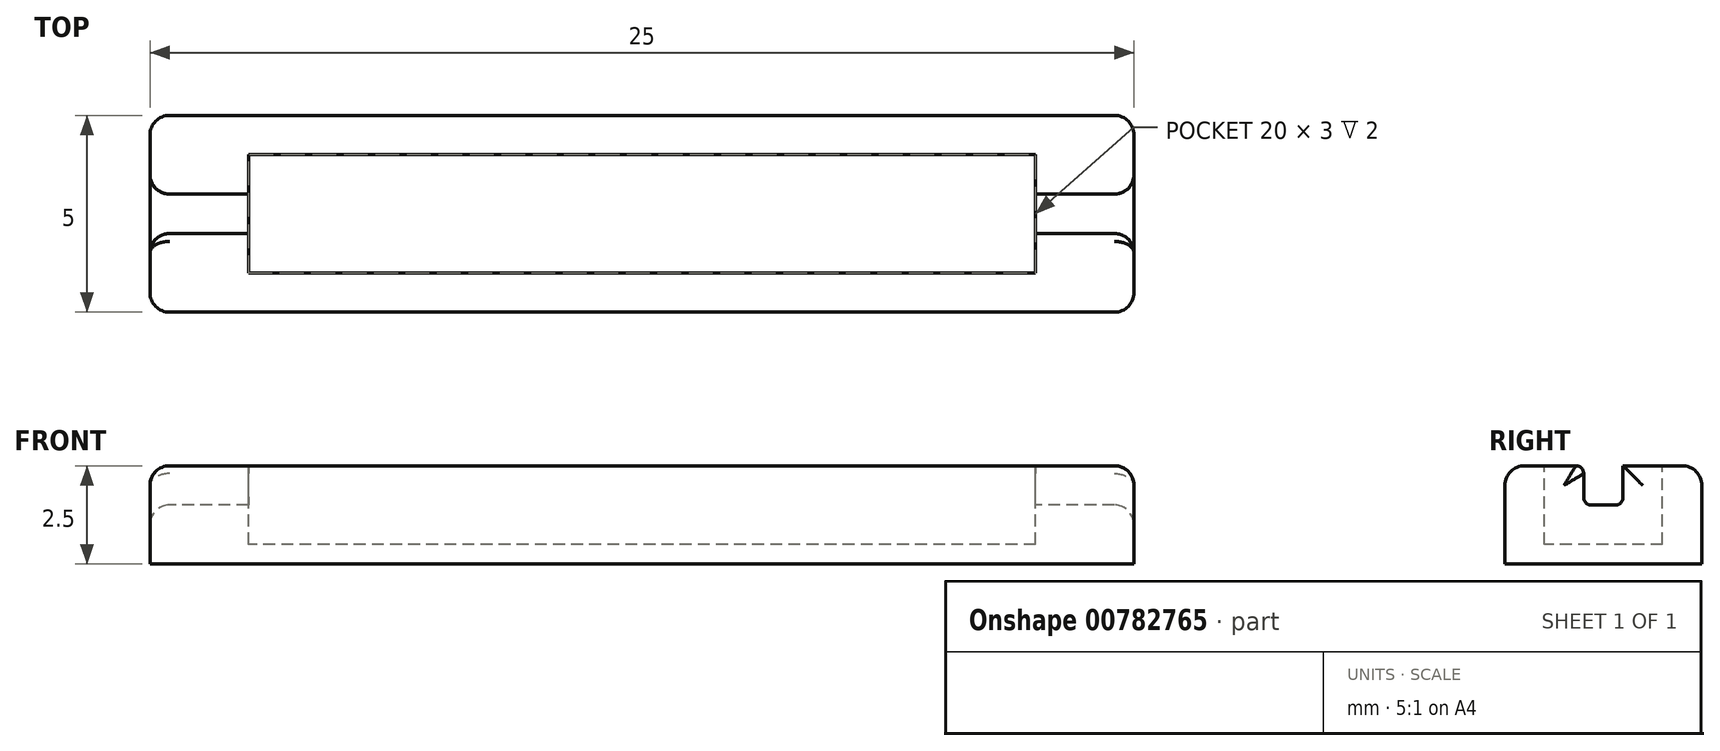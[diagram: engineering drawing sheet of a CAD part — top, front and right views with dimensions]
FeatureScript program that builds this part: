
annotation { "Feature Type Name" : "Feature", "Feature Type Description" : "" }
export const myFeature = defineFeature(function(context is Context, id is Id, definition is map)
    precondition{}
    {
        {
            var Q0;
            Q0=qCreatedBy(makeId("Top.planeOp"),FACE);
            var sketch = newSketch(context, id + "F0", { "sketchPlane" : qUnion([Q0])});
            skLineSegment(sketch, "E0.bottom", {"start": v(12.5, 2.5) * mm, "end": v(-12.5, 2.5) * mm});
            skLineSegment(sketch, "E0.top", {"start": v(12.5, -2.5) * mm, "end": v(-12.5, -2.5) * mm});
            skLineSegment(sketch, "E0.left", {"start": v(12.5, 2.5) * mm, "end": v(12.5, -2.5) * mm});
            skLineSegment(sketch, "E0.right", {"start": v(-12.5, 2.5) * mm, "end": v(-12.5, -2.5) * mm});
            skPoint(sketch, "E0.middle", {"position": v(0, 0) * mm});
            skSolve(sketch);
        }
        {
            var Q0;
            Q0=makeQuery(id+"F0.imprint","IMPRINT",FACE,{"disambiguationData":[TD([[makeQuery(id+"F0.imprint","IMPRINT",EDGE,{"derivedFrom":sQuery(id+"F0.wireOp",EDGE,"E0.bottom")}),1.0]])]});
            extrude(context, id + "F1", {"entities" : qUnion([Q0]), "depth" : 2.5 * mm, "offsetDistance" : 25.4 * mm});
        }
        {
            var Q0;
            Q0=makeQuery(id+"F1.opExtrude","CAP_FACE",FACE,{"disambiguationData":[OSD([sQuery(id+"F0.wireOp",EDGE,"E0.bottom"),sQuery(id+"F0.wireOp",EDGE,"E0.top"),sQuery(id+"F0.wireOp",EDGE,"E0.left"),sQuery(id+"F0.wireOp",EDGE,"E0.right")])],"isStart":false});
            var sketch = newSketch(context, id + "F2", { "sketchPlane" : qUnion([Q0])});
            skLineSegment(sketch, "E1.bottom", {"start": v(10, 1.5) * mm, "end": v(-10, 1.5) * mm});
            skLineSegment(sketch, "E1.top", {"start": v(10, -1.5) * mm, "end": v(-10, -1.5) * mm});
            skLineSegment(sketch, "E1.left", {"start": v(10, 1.5) * mm, "end": v(10, -1.5) * mm});
            skLineSegment(sketch, "E1.right", {"start": v(-10, 1.5) * mm, "end": v(-10, -1.5) * mm});
            skPoint(sketch, "E1.middle", {"position": v(0, 0) * mm});
            skSolve(sketch);
        }
        {
            var Q0;
            Q0=makeQuery(id+"F2.imprint","IMPRINT",FACE,{"disambiguationData":[TD([[makeQuery(id+"F2.imprint","IMPRINT",EDGE,{"derivedFrom":sQuery(id+"F2.wireOp",EDGE,"E1.bottom")}),1.0]])]});
            extrude(context, id + "F3", {"entities" : qUnion([Q0]), "operationType" : NewBodyOperationType.REMOVE, "oppositeDirection" : true, "depth" : 2 * mm, "offsetDistance" : 25.4 * mm});
        }
        {
            var Q0;
            Q0=makeQuery(id+"F1.opExtrude","CAP_FACE",FACE,{"disambiguationData":[OSD([sQuery(id+"F0.wireOp",EDGE,"E0.bottom"),sQuery(id+"F0.wireOp",EDGE,"E0.top"),sQuery(id+"F0.wireOp",EDGE,"E0.left"),sQuery(id+"F0.wireOp",EDGE,"E0.right")])],"isStart":false});
            var sketch = newSketch(context, id + "F4", { "sketchPlane" : qUnion([Q0])});
            skLineSegment(sketch, "E2.bottom", {"start": v(12.5, -0.5) * mm, "end": v(-12.5, -0.5) * mm});
            skLineSegment(sketch, "E2.top", {"start": v(12.5, 0.5) * mm, "end": v(-12.5, 0.5) * mm});
            skLineSegment(sketch, "E2.left", {"start": v(12.5, -0.5) * mm, "end": v(12.5, 0.5) * mm});
            skLineSegment(sketch, "E2.right", {"start": v(-12.5, -0.5) * mm, "end": v(-12.5, 0.5) * mm});
            skPoint(sketch, "E2.middle", {"position": v(0, 0) * mm});
            skSolve(sketch);
        }
        {
            var Q0;
            {var subQ0=sQuery(id+"F4.wireOp",EDGE,"E2.right");Q0=makeQuery(id+"F4.imprint","IMPRINT",FACE,{"disambiguationData":[TD([[makeQuery(id+"F4.imprint","IMPRINT",EDGE,{"derivedFrom":subQ0}),1.0]])]});}
            var Q1;
            {var subQ0=sQuery(id+"F4.wireOp",EDGE,"E2.left");Q1=makeQuery(id+"F4.imprint","IMPRINT",FACE,{"disambiguationData":[TD([[makeQuery(id+"F4.imprint","IMPRINT",EDGE,{"derivedFrom":subQ0}),-1.0]])]});}
            extrude(context, id + "F5", {"entities" : qUnion([Q0, Q1]), "operationType" : NewBodyOperationType.REMOVE, "oppositeDirection" : true, "depth" : 1 * mm, "offsetDistance" : 25.4 * mm});
        }
        {
            var Q0;
            {var subQ0=sQuery(id+"F4.wireOp",EDGE,"E2.bottom");Q0=makeQuery(id+"F5.boolean.opBoolean","COPY",EDGE,{"derivedFrom":makeQuery(id+"F5.opExtrude","CAP_EDGE",EDGE,{"disambiguationData":[OSD([subQ0]),TDD([makeQuery(id+"F4.imprint","IMPRINT",EDGE,{"disambiguationData":[TD([[makeQuery(id+"F4.imprint","INTERSECT",VERTEX,{"derivedFrom":[makeQuery(id+"F3.boolean.opBoolean","COPY",EDGE,{"derivedFrom":makeQuery(id+"F3.opExtrude","CAP_EDGE",EDGE,{"disambiguationData":[OSD([sQuery(id+"F2.wireOp",EDGE,"E1.right")])],"isStart":true})}),subQ0]}),-1.0]])],"derivedFrom":subQ0})])],"isStart":false})});}
            var Q1;
            {var subQ0=sQuery(id+"F4.wireOp",EDGE,"E2.top");Q1=makeQuery(id+"F5.boolean.opBoolean","COPY",EDGE,{"derivedFrom":makeQuery(id+"F5.opExtrude","CAP_EDGE",EDGE,{"disambiguationData":[OSD([subQ0]),TDD([makeQuery(id+"F4.imprint","IMPRINT",EDGE,{"disambiguationData":[TD([[makeQuery(id+"F4.imprint","INTERSECT",VERTEX,{"derivedFrom":[makeQuery(id+"F3.boolean.opBoolean","COPY",EDGE,{"derivedFrom":makeQuery(id+"F3.opExtrude","CAP_EDGE",EDGE,{"disambiguationData":[OSD([sQuery(id+"F2.wireOp",EDGE,"E1.right")])],"isStart":true})}),subQ0]}),-1.0]])],"derivedFrom":subQ0})])],"isStart":false})});}
            var Q2;
            Q2=makeQuery(id+"F5.boolean.opBoolean","COPY",EDGE,{"derivedFrom":makeQuery(id+"F5.opExtrude","SWEPT_EDGE",EDGE,{"disambiguationData":[OSD([sQuery(id+"F2.wireOp",EDGE,"E1.right"),sQuery(id+"F4.wireOp",EDGE,"E2.bottom")])]})});
            var Q3;
            {var subQ0=sQuery(id+"F4.wireOp",EDGE,"E2.bottom");Q3=makeQuery(id+"F5.boolean.opBoolean","COPY",EDGE,{"derivedFrom":makeQuery(id+"F5.opExtrude","CAP_EDGE",EDGE,{"disambiguationData":[OSD([subQ0]),TDD([makeQuery(id+"F4.imprint","IMPRINT",EDGE,{"disambiguationData":[TD([[makeQuery(id+"F4.imprint","INTERSECT",VERTEX,{"derivedFrom":[makeQuery(id+"F3.boolean.opBoolean","COPY",EDGE,{"derivedFrom":makeQuery(id+"F3.opExtrude","CAP_EDGE",EDGE,{"disambiguationData":[OSD([sQuery(id+"F2.wireOp",EDGE,"E1.left")])],"isStart":true})}),subQ0]}),1.0]])],"derivedFrom":subQ0})])],"isStart":false})});}
            var Q4;
            {var subQ0=sQuery(id+"F4.wireOp",EDGE,"E2.top");Q4=makeQuery(id+"F5.boolean.opBoolean","COPY",EDGE,{"derivedFrom":makeQuery(id+"F5.opExtrude","CAP_EDGE",EDGE,{"disambiguationData":[OSD([subQ0]),TDD([makeQuery(id+"F4.imprint","IMPRINT",EDGE,{"disambiguationData":[TD([[makeQuery(id+"F4.imprint","INTERSECT",VERTEX,{"derivedFrom":[makeQuery(id+"F3.boolean.opBoolean","COPY",EDGE,{"derivedFrom":makeQuery(id+"F3.opExtrude","CAP_EDGE",EDGE,{"disambiguationData":[OSD([sQuery(id+"F2.wireOp",EDGE,"E1.left")])],"isStart":true})}),subQ0]}),1.0]])],"derivedFrom":subQ0})])],"isStart":false})});}
            var Q5;
            Q5=makeQuery(id+"F5.boolean.opBoolean","COPY",EDGE,{"derivedFrom":makeQuery(id+"F5.opExtrude","CAP_EDGE",EDGE,{"disambiguationData":[OSD([sQuery(id+"F2.wireOp",EDGE,"E1.left")])],"isStart":false})});
            var Q6;
            Q6=makeQuery(id+"F5.boolean.opBoolean","COPY",EDGE,{"derivedFrom":makeQuery(id+"F5.opExtrude","SWEPT_EDGE",EDGE,{"disambiguationData":[OSD([sQuery(id+"F0.wireOp",EDGE,"E0.left"),sQuery(id+"F4.wireOp",EDGE,"E2.bottom"),sQuery(id+"F4.wireOp",EDGE,"E2.left")])]})});
            var Q7;
            Q7=makeQuery(id+"F5.boolean.opBoolean","COPY",EDGE,{"derivedFrom":makeQuery(id+"F5.opExtrude","SWEPT_EDGE",EDGE,{"disambiguationData":[OSD([sQuery(id+"F0.wireOp",EDGE,"E0.right"),sQuery(id+"F4.wireOp",EDGE,"E2.top"),sQuery(id+"F4.wireOp",EDGE,"E2.right")])]})});
            var Q8;
            {var subQ0=sQuery(id+"F4.wireOp",EDGE,"E2.top");Q8=makeQuery(id+"F5.boolean.opBoolean","COPY",EDGE,{"derivedFrom":makeQuery(id+"F5.opExtrude","CAP_EDGE",EDGE,{"disambiguationData":[OSD([subQ0]),TDD([makeQuery(id+"F4.imprint","IMPRINT",EDGE,{"disambiguationData":[TD([[makeQuery(id+"F4.imprint","INTERSECT",VERTEX,{"derivedFrom":[makeQuery(id+"F3.boolean.opBoolean","COPY",EDGE,{"derivedFrom":makeQuery(id+"F3.opExtrude","CAP_EDGE",EDGE,{"disambiguationData":[OSD([sQuery(id+"F2.wireOp",EDGE,"E1.right")])],"isStart":true})}),subQ0]}),-1.0]])],"derivedFrom":subQ0})])],"isStart":true})});}
            var Q9;
            {var subQ0=sQuery(id+"F4.wireOp",EDGE,"E2.bottom");Q9=makeQuery(id+"F5.boolean.opBoolean","COPY",EDGE,{"derivedFrom":makeQuery(id+"F5.opExtrude","CAP_EDGE",EDGE,{"disambiguationData":[OSD([subQ0]),TDD([makeQuery(id+"F4.imprint","IMPRINT",EDGE,{"disambiguationData":[TD([[makeQuery(id+"F4.imprint","INTERSECT",VERTEX,{"derivedFrom":[makeQuery(id+"F3.boolean.opBoolean","COPY",EDGE,{"derivedFrom":makeQuery(id+"F3.opExtrude","CAP_EDGE",EDGE,{"disambiguationData":[OSD([sQuery(id+"F2.wireOp",EDGE,"E1.right")])],"isStart":true})}),subQ0]}),-1.0]])],"derivedFrom":subQ0})])],"isStart":true})});}
            var Q10;
            {var subQ0=sQuery(id+"F4.wireOp",EDGE,"E2.top");Q10=makeQuery(id+"F5.boolean.opBoolean","COPY",EDGE,{"derivedFrom":makeQuery(id+"F5.opExtrude","CAP_EDGE",EDGE,{"disambiguationData":[OSD([subQ0]),TDD([makeQuery(id+"F4.imprint","IMPRINT",EDGE,{"disambiguationData":[TD([[makeQuery(id+"F4.imprint","INTERSECT",VERTEX,{"derivedFrom":[makeQuery(id+"F3.boolean.opBoolean","COPY",EDGE,{"derivedFrom":makeQuery(id+"F3.opExtrude","CAP_EDGE",EDGE,{"disambiguationData":[OSD([sQuery(id+"F2.wireOp",EDGE,"E1.left")])],"isStart":true})}),subQ0]}),1.0]])],"derivedFrom":subQ0})])],"isStart":true})});}
            var Q11;
            {var subQ0=sQuery(id+"F4.wireOp",EDGE,"E2.bottom");Q11=makeQuery(id+"F5.boolean.opBoolean","COPY",EDGE,{"derivedFrom":makeQuery(id+"F5.opExtrude","CAP_EDGE",EDGE,{"disambiguationData":[OSD([subQ0]),TDD([makeQuery(id+"F4.imprint","IMPRINT",EDGE,{"disambiguationData":[TD([[makeQuery(id+"F4.imprint","INTERSECT",VERTEX,{"derivedFrom":[makeQuery(id+"F3.boolean.opBoolean","COPY",EDGE,{"derivedFrom":makeQuery(id+"F3.opExtrude","CAP_EDGE",EDGE,{"disambiguationData":[OSD([sQuery(id+"F2.wireOp",EDGE,"E1.left")])],"isStart":true})}),subQ0]}),1.0]])],"derivedFrom":subQ0})])],"isStart":true})});}
            var Q12;
            {var subQ2=sQuery(id+"F2.wireOp",EDGE,"E1.right");var subQ3=makeQuery(id+"F3.boolean.opBoolean","COPY",EDGE,{"derivedFrom":makeQuery(id+"F3.opExtrude","CAP_EDGE",EDGE,{"disambiguationData":[OSD([subQ2])],"isStart":true})});Q12=makeQuery(id+"F5.boolean.opBoolean","SPLIT",EDGE,{"disambiguationData":[TD([makeQuery(id+"F3.boolean.opBoolean","COPY",FACE,{"derivedFrom":makeQuery(id+"F3.opExtrude","SWEPT_FACE",FACE,{"disambiguationData":[OSD([sQuery(id+"F2.wireOp",EDGE,"E1.bottom")])]})})])],"derivedFrom":subQ3});}
            var Q13;
            {var subQ1=sQuery(id+"F2.wireOp",EDGE,"E1.left");var subQ3=makeQuery(id+"F3.boolean.opBoolean","COPY",EDGE,{"derivedFrom":makeQuery(id+"F3.opExtrude","CAP_EDGE",EDGE,{"disambiguationData":[OSD([subQ1])],"isStart":true})});Q13=makeQuery(id+"F5.boolean.opBoolean","SPLIT",EDGE,{"disambiguationData":[TD([makeQuery(id+"F3.boolean.opBoolean","COPY",FACE,{"derivedFrom":makeQuery(id+"F3.opExtrude","SWEPT_FACE",FACE,{"disambiguationData":[OSD([sQuery(id+"F2.wireOp",EDGE,"E1.bottom")])]})})])],"derivedFrom":subQ3});}
            var Q14;
            {var subQ1=sQuery(id+"F2.wireOp",EDGE,"E1.left");var subQ3=makeQuery(id+"F3.boolean.opBoolean","COPY",EDGE,{"derivedFrom":makeQuery(id+"F3.opExtrude","CAP_EDGE",EDGE,{"disambiguationData":[OSD([subQ1])],"isStart":true})});Q14=makeQuery(id+"F5.boolean.opBoolean","SPLIT",EDGE,{"disambiguationData":[TD([makeQuery(id+"F3.boolean.opBoolean","COPY",FACE,{"derivedFrom":makeQuery(id+"F3.opExtrude","SWEPT_FACE",FACE,{"disambiguationData":[OSD([sQuery(id+"F2.wireOp",EDGE,"E1.top")])]})})])],"derivedFrom":subQ3});}
            var Q15;
            {var subQ1=sQuery(id+"F2.wireOp",EDGE,"E1.right");var subQ3=makeQuery(id+"F3.boolean.opBoolean","COPY",EDGE,{"derivedFrom":makeQuery(id+"F3.opExtrude","CAP_EDGE",EDGE,{"disambiguationData":[OSD([subQ1])],"isStart":true})});Q15=makeQuery(id+"F5.boolean.opBoolean","SPLIT",EDGE,{"disambiguationData":[TD([makeQuery(id+"F3.boolean.opBoolean","COPY",FACE,{"derivedFrom":makeQuery(id+"F3.opExtrude","SWEPT_FACE",FACE,{"disambiguationData":[OSD([sQuery(id+"F2.wireOp",EDGE,"E1.top")])]})})])],"derivedFrom":subQ3});}
            fillet(context, id + "F6", {"entities" : qUnion([Q0, Q1, Q2, Q3, Q4, Q5, Q6, Q7, Q8, Q9, Q10, Q11, Q12, Q13, Q14, Q15]), "radius" : 0.2 * mm, "tangentPropagation" : true, "allowEdgeOverflow" : false});
        }
        {
            var Q0;
            Q0=makeQuery(id+"F1.opExtrude","CAP_EDGE",EDGE,{"disambiguationData":[OSD([sQuery(id+"F0.wireOp",EDGE,"E0.top")])],"isStart":false});
            var Q1;
            {var subQ0=sQuery(id+"F0.wireOp",EDGE,"E0.right");var subQ1=sQuery(id+"F0.wireOp",EDGE,"E0.top");var subQ3=makeQuery(id+"F1.opExtrude","CAP_EDGE",EDGE,{"disambiguationData":[OSD([subQ0])],"isStart":false});Q1=makeQuery(id+"F5.boolean.opBoolean","SPLIT",EDGE,{"disambiguationData":[TD([makeQuery(id+"F1.opExtrude","SWEPT_FACE",FACE,{"disambiguationData":[OSD([subQ1])]})])],"derivedFrom":subQ3});}
            var Q2;
            Q2=makeQuery(id+"F1.opExtrude","SWEPT_EDGE",EDGE,{"disambiguationData":[OSD([sQuery(id+"F0.wireOp",EDGE,"E0.top"),sQuery(id+"F0.wireOp",EDGE,"E0.right")])]});
            var Q3;
            Q3=makeQuery(id+"F1.opExtrude","SWEPT_EDGE",EDGE,{"disambiguationData":[OSD([sQuery(id+"F0.wireOp",EDGE,"E0.top"),sQuery(id+"F0.wireOp",EDGE,"E0.left")])]});
            var Q4;
            {var subQ0=sQuery(id+"F0.wireOp",EDGE,"E0.left");var subQ1=sQuery(id+"F0.wireOp",EDGE,"E0.top");var subQ3=makeQuery(id+"F1.opExtrude","CAP_EDGE",EDGE,{"disambiguationData":[OSD([subQ0])],"isStart":false});Q4=makeQuery(id+"F5.boolean.opBoolean","SPLIT",EDGE,{"disambiguationData":[TD([makeQuery(id+"F1.opExtrude","SWEPT_FACE",FACE,{"disambiguationData":[OSD([subQ1])]})])],"derivedFrom":subQ3});}
            var Q5;
            Q5=makeQuery(id+"F1.opExtrude","CAP_EDGE",EDGE,{"disambiguationData":[OSD([sQuery(id+"F0.wireOp",EDGE,"E0.bottom")])],"isStart":false});
            var Q6;
            Q6=makeQuery(id+"F1.opExtrude","SWEPT_EDGE",EDGE,{"disambiguationData":[OSD([sQuery(id+"F0.wireOp",EDGE,"E0.bottom"),sQuery(id+"F0.wireOp",EDGE,"E0.right")])]});
            var Q7;
            Q7=makeQuery(id+"F1.opExtrude","SWEPT_EDGE",EDGE,{"disambiguationData":[OSD([sQuery(id+"F0.wireOp",EDGE,"E0.bottom"),sQuery(id+"F0.wireOp",EDGE,"E0.left")])]});
            var Q8;
            {var subQ0=sQuery(id+"F0.wireOp",EDGE,"E0.bottom");var subQ1=sQuery(id+"F0.wireOp",EDGE,"E0.right");var subQ3=makeQuery(id+"F1.opExtrude","CAP_EDGE",EDGE,{"disambiguationData":[OSD([subQ1])],"isStart":false});Q8=makeQuery(id+"F5.boolean.opBoolean","SPLIT",EDGE,{"disambiguationData":[TD([makeQuery(id+"F1.opExtrude","SWEPT_FACE",FACE,{"disambiguationData":[OSD([subQ0])]})])],"derivedFrom":subQ3});}
            var Q9;
            {var subQ0=sQuery(id+"F0.wireOp",EDGE,"E0.bottom");var subQ1=sQuery(id+"F0.wireOp",EDGE,"E0.left");var subQ3=makeQuery(id+"F1.opExtrude","CAP_EDGE",EDGE,{"disambiguationData":[OSD([subQ1])],"isStart":false});Q9=makeQuery(id+"F5.boolean.opBoolean","SPLIT",EDGE,{"disambiguationData":[TD([makeQuery(id+"F1.opExtrude","SWEPT_FACE",FACE,{"disambiguationData":[OSD([subQ0])]})])],"derivedFrom":subQ3});}
            fillet(context, id + "F7", {"entities" : qUnion([Q0, Q1, Q2, Q3, Q4, Q5, Q6, Q7, Q8, Q9]), "radius" : 0.5 * mm, "tangentPropagation" : true, "allowEdgeOverflow" : false});
        }
    });
